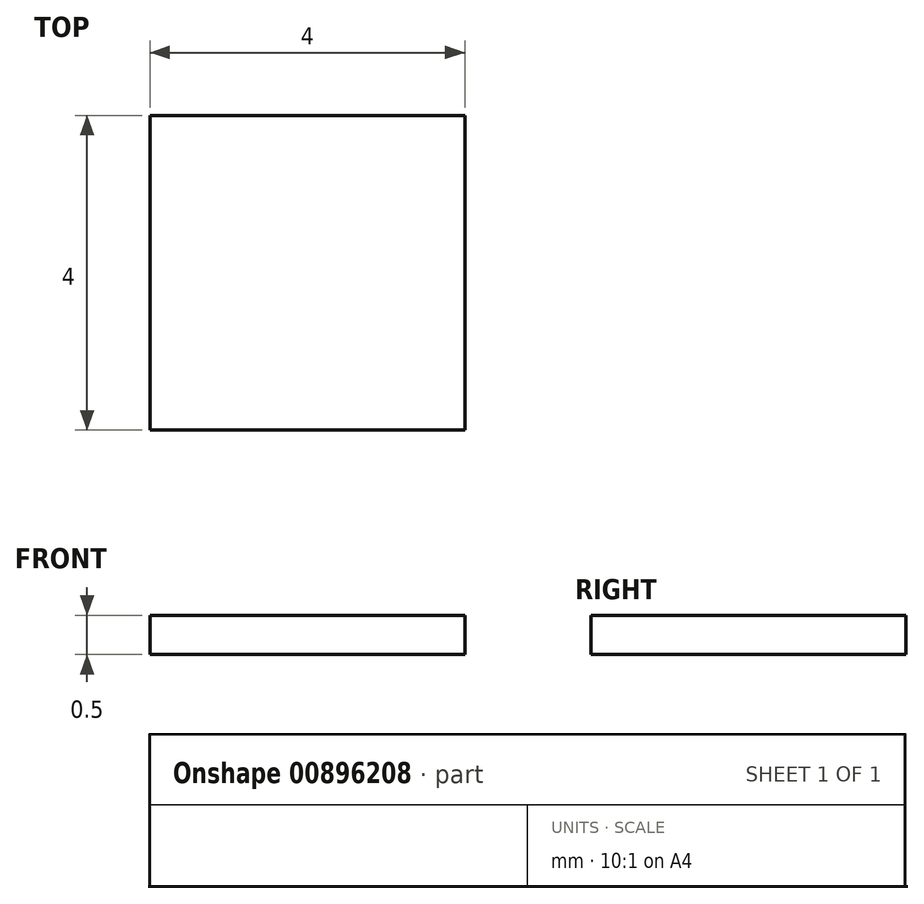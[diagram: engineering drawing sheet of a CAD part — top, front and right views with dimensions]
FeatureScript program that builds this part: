
annotation { "Feature Type Name" : "Feature", "Feature Type Description" : "" }
export const myFeature = defineFeature(function(context is Context, id is Id, definition is map)
    precondition{}
    {
        {
            var Q0;
            Q0=qCreatedBy(makeId("Top.planeOp"),FACE);
            var sketch = newSketch(context, id + "F0", { "sketchPlane" : qUnion([Q0])});
            skLineSegment(sketch, "E0.bottom", {"start": v(2, 2) * mm, "end": v(-2, 2) * mm});
            skLineSegment(sketch, "E0.top", {"start": v(2, -2) * mm, "end": v(-2, -2) * mm});
            skLineSegment(sketch, "E0.left", {"start": v(2, 2) * mm, "end": v(2, -2) * mm});
            skLineSegment(sketch, "E0.right", {"start": v(-2, 2) * mm, "end": v(-2, -2) * mm});
            skPoint(sketch, "E0.middle", {"position": v(0, 0) * mm});
            skSolve(sketch);
        }
        {
            var Q0;
            Q0 = qSketchRegion(id + "F0", true);
            extrude(context, id + "F1", {"entities" : qUnion([Q0]), "depth" : 0.5 * mm, "offsetDistance" : 25 * mm});
        }
    });
